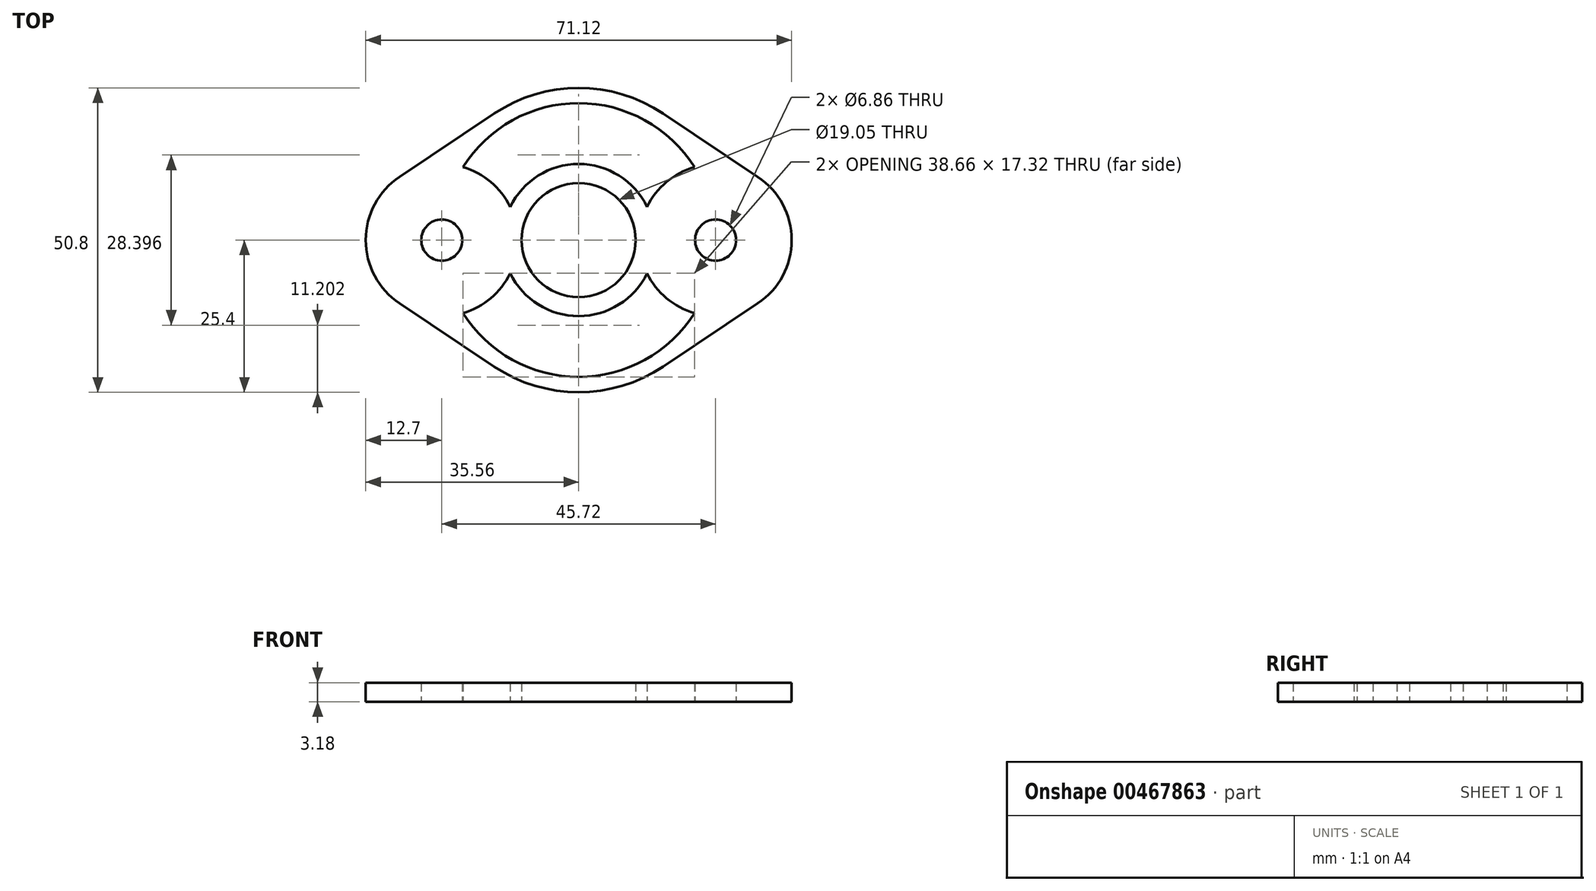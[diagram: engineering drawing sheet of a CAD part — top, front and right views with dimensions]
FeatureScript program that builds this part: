
annotation { "Feature Type Name" : "Feature", "Feature Type Description" : "" }
export const myFeature = defineFeature(function(context is Context, id is Id, definition is map)
    precondition{}
    {
        {
            var Q0;
            Q0=qCreatedBy(makeId("Top.planeOp"),FACE);
            var sketch = newSketch(context, id + "F0", { "sketchPlane" : qUnion([Q0])});
            skArc(sketch, "E0", {"start": v(-7.06, 10.56) * mm, "mid": v(-12.7, 0) * mm, "end": v(-7.06, -10.56) * mm});
            skLineSegment(sketch, "E1", {"start": v(0, 0) * mm, "end": v(45.72, 0) * mm, "construction": true});
            skArc(sketch, "E2", {"start": v(52.78, -10.56) * mm, "mid": v(58.42, 0) * mm, "end": v(52.78, 10.56) * mm});
            skArc(sketch, "E3", {"start": v(8.75, -21.12) * mm, "mid": v(22.86, -25.4) * mm, "end": v(36.97, -21.12) * mm});
            skLineSegment(sketch, "E4", {"start": v(-7.06, -10.56) * mm, "end": v(8.75, -21.12) * mm});
            skLineSegment(sketch, "E5", {"start": v(-7.06, 10.56) * mm, "end": v(8.75, 21.12) * mm});
            skLineSegment(sketch, "E6", {"start": v(36.97, 21.12) * mm, "end": v(52.78, 10.56) * mm});
            skLineSegment(sketch, "E7", {"start": v(36.97, -21.12) * mm, "end": v(52.78, -10.56) * mm});
            skArc(sketch, "E8", {"start": v(34.3, 5.54) * mm, "mid": v(22.86, 12.7) * mm, "end": v(11.43, 5.54) * mm});
            skArc(sketch, "E9.trimOffspring", {"start": v(3.53, -12.2) * mm, "mid": v(8.19, -9.7) * mm, "end": v(11.43, -5.54) * mm});
            skArc(sketch, "E10.trimOffspring", {"start": v(36.97, 21.12) * mm, "mid": v(22.86, 25.4) * mm, "end": v(8.75, 21.12) * mm});
            skArc(sketch, "E11.trimOffspring", {"start": v(42.2, 12.2) * mm, "mid": v(37.53, 9.7) * mm, "end": v(34.29, 5.54) * mm});
            skArc(sketch, "E12.trimOffspring", {"start": v(34.3, -5.54) * mm, "mid": v(37.53, -9.7) * mm, "end": v(42.2, -12.2) * mm});
            skArc(sketch, "E13.trimOffspring", {"start": v(11.43, -5.54) * mm, "mid": v(22.86, -12.7) * mm, "end": v(34.3, -5.54) * mm});
            skArc(sketch, "E14.trimOffspring", {"start": v(11.43, 5.54) * mm, "mid": v(8.19, 9.7) * mm, "end": v(3.53, 12.2) * mm});
            skArc(sketch, "E15", {"start": v(3.53, -12.2) * mm, "mid": v(22.86, -22.86) * mm, "end": v(42.2, -12.2) * mm});
            skArc(sketch, "E16.trimOffspring", {"start": v(42.2, 12.2) * mm, "mid": v(22.86, 22.86) * mm, "end": v(3.53, 12.2) * mm});
            skCircle(sketch, "E17", {"center": v(22.86, 0) * mm, "radius": 9.53 * mm});
            skCircle(sketch, "E18", {"center": v(0, 0) * mm, "radius": 3.43 * mm});
            skCircle(sketch, "E19", {"center": v(45.72, 0) * mm, "radius": 3.43 * mm});
            skSolve(sketch);
        }
        {
            var Q0;
            Q0=makeQuery(id+"F0.imprint","IMPRINT",FACE,{"disambiguationData":[TD([[makeQuery(id+"F0.imprint","IMPRINT",EDGE,{"derivedFrom":sQuery(id+"F0.wireOp",EDGE,"E0")}),1.0]])]});
            extrude(context, id + "F1", {"entities" : qUnion([Q0]), "depth" : 3.17 * mm});
        }
    });
